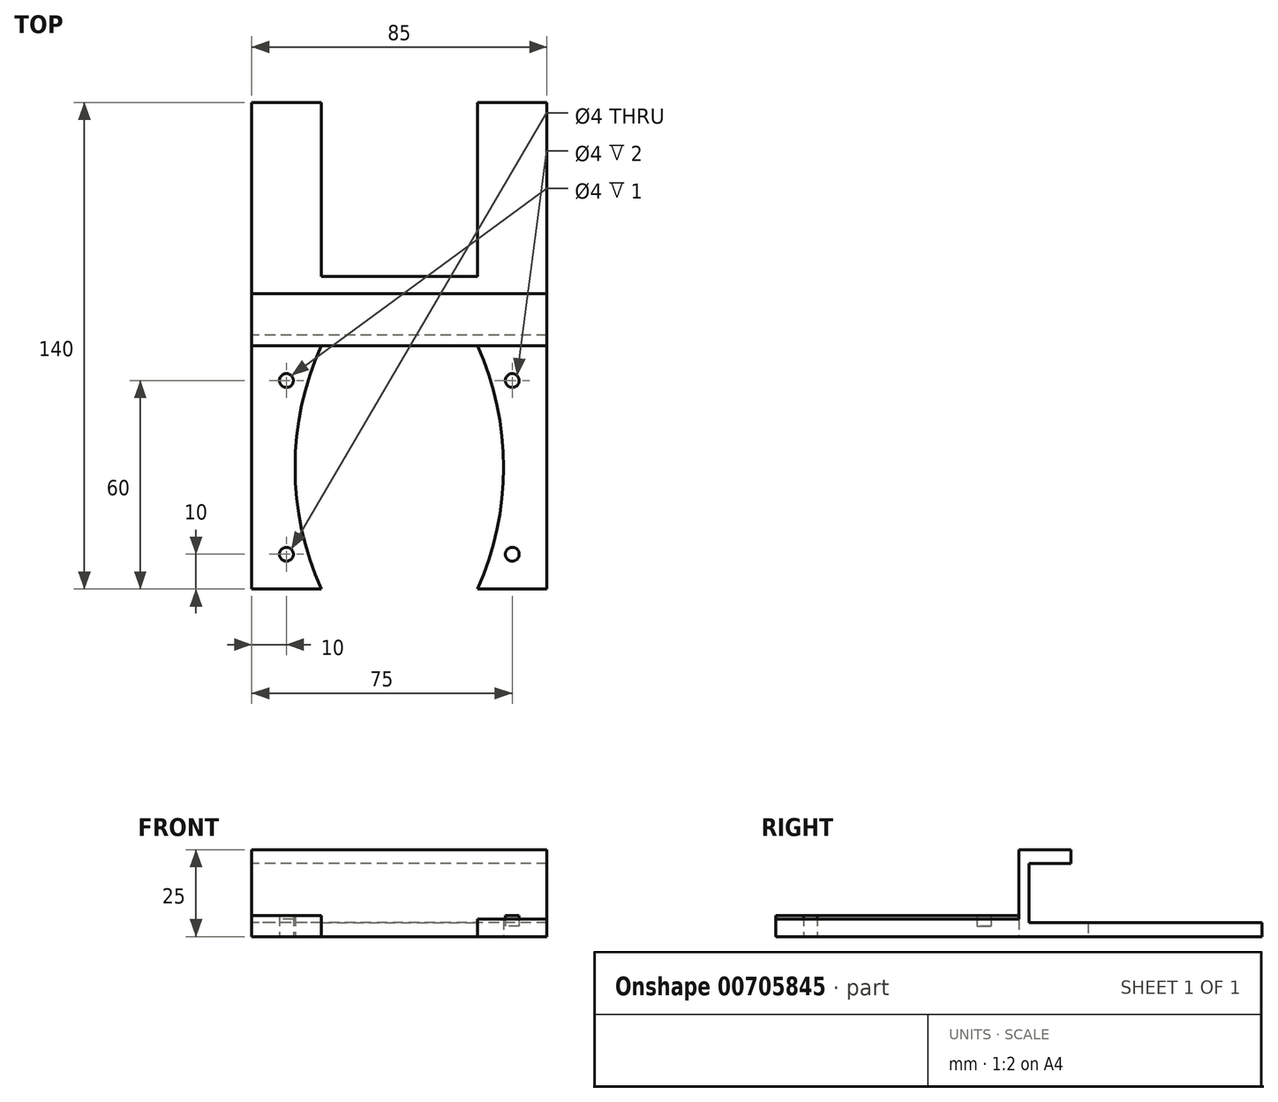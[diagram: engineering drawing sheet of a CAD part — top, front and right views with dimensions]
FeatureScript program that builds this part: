
annotation { "Feature Type Name" : "Feature", "Feature Type Description" : "" }
export const myFeature = defineFeature(function(context is Context, id is Id, definition is map)
    precondition{}
    {
        {
            var Q0;
            Q0=qCreatedBy(makeId("Top.planeOp"),FACE);
            var sketch = newSketch(context, id + "F0", { "sketchPlane" : qUnion([Q0])});
            skLineSegment(sketch, "E0", {"start": v(0, 0) * mm, "end": v(0, 70) * mm, "construction": true});
            skLineSegment(sketch, "E1", {"start": v(0, 0) * mm, "end": v(0, -70) * mm, "construction": true});
            skLineSegment(sketch, "E2", {"start": v(-22.5, 0) * mm, "end": v(22.5, 0) * mm});
            skLineSegment(sketch, "E3", {"start": v(22.5, -70) * mm, "end": v(-22.5, -70) * mm});
            skPoint(sketch, "E4", {"position": v(0, -35) * mm});
            skLineSegment(sketch, "E5", {"start": v(30, -35) * mm, "end": v(-30, -35) * mm, "construction": true});
            skArc(sketch, "E6", {"start": v(-22.5, 0) * mm, "mid": v(-30, -35) * mm, "end": v(-22.5, -70) * mm});
            skLineSegment(sketch, "E7", {"start": v(-22.5, 0) * mm, "end": v(-42.5, 0) * mm});
            skPoint(sketch, "E8", {"position": v(-32.5, 0) * mm});
            skPoint(sketch, "E9", {"position": v(-32.5, -10) * mm});
            skCircle(sketch, "E10", {"center": v(-32.5, -10) * mm, "radius": 2 * mm});
            skCircle(sketch, "E11.MirrorC", {"center": v(-32.5, -60) * mm, "radius": 2 * mm});
            skLineSegment(sketch, "E12.MirrorCS", {"start": v(-22.5, -70) * mm, "end": v(-42.5, -70) * mm});
            skLineSegment(sketch, "E13", {"start": v(-42.5, -70) * mm, "end": v(-42.5, 0) * mm});
            skLineSegment(sketch, "E14.MirrorCS", {"start": v(-42.5, 70) * mm, "end": v(-42.5, 0) * mm});
            skLineSegment(sketch, "E15.MirrorCS", {"start": v(-22.5, 70) * mm, "end": v(-42.5, 70) * mm});
            skLineSegment(sketch, "E16", {"start": v(0, 20) * mm, "end": v(-22.5, 20) * mm});
            skLineSegment(sketch, "E17", {"start": v(-22.5, 20) * mm, "end": v(-22.5, 70) * mm});
            skCircle(sketch, "E18.MirrorC", {"center": v(32.5, -10) * mm, "radius": 2 * mm});
            skLineSegment(sketch, "E19.MirrorCS", {"start": v(22.5, 20) * mm, "end": v(22.5, 70) * mm});
            skPoint(sketch, "E20.MirrorP", {"position": v(32.5, 0) * mm});
            skLineSegment(sketch, "E21.MirrorCS", {"start": v(42.5, 70) * mm, "end": v(42.5, 0) * mm});
            skLineSegment(sketch, "E22.MirrorCS", {"start": v(22.5, 70) * mm, "end": v(42.5, 70) * mm});
            skLineSegment(sketch, "E23.MirrorCS", {"start": v(42.5, -70) * mm, "end": v(42.5, 0) * mm});
            skArc(sketch, "E24.MirrorCS", {"start": v(22.5, 0) * mm, "mid": v(30, -35) * mm, "end": v(22.5, -70) * mm});
            skLineSegment(sketch, "E25.MirrorCS", {"start": v(22.5, -70) * mm, "end": v(42.5, -70) * mm});
            skLineSegment(sketch, "E26.MirrorCS", {"start": v(22.5, 0) * mm, "end": v(42.5, 0) * mm});
            skCircle(sketch, "E27.MirrorC", {"center": v(32.5, -60) * mm, "radius": 2 * mm});
            skLineSegment(sketch, "E28", {"start": v(0, 20) * mm, "end": v(22.5, 20) * mm});
            skSolve(sketch);
        }
        {
            var Q0;
            Q0=makeQuery(id+"F0.imprint","IMPRINT",FACE,{"disambiguationData":[TD([[makeQuery(id+"F0.imprint","IMPRINT",EDGE,{"derivedFrom":sQuery(id+"F0.wireOp",EDGE,"E2")}),1.0]])]});
            extrude(context, id + "F1", {"entities" : qUnion([Q0]), "depth" : 25 * mm, "offsetDistance" : 25 * mm});
        }
        {
            var Q0;
            Q0=makeQuery(id+"F0.imprint","IMPRINT",FACE,{"disambiguationData":[TD([[makeQuery(id+"F0.imprint","IMPRINT",EDGE,{"derivedFrom":sQuery(id+"F0.wireOp",EDGE,"E6")}),-1.0]])]});
            var Q1;
            Q1=makeQuery(id+"F0.imprint","IMPRINT",FACE,{"disambiguationData":[TD([[makeQuery(id+"F0.imprint","IMPRINT",EDGE,{"derivedFrom":sQuery(id+"F0.wireOp",EDGE,"E18.MirrorC")}),1.0]])]});
            extrude(context, id + "F2", {"entities" : qUnion([Q0, Q1]), "operationType" : NewBodyOperationType.ADD, "depth" : 3 * mm, "offsetDistance" : 25 * mm});
        }
        {
            var Q0;
            Q0=makeQuery(id+"F0.imprint","IMPRINT",FACE,{"disambiguationData":[TD([[makeQuery(id+"F0.imprint","IMPRINT",EDGE,{"derivedFrom":sQuery(id+"F0.wireOp",EDGE,"E10")}),1.0]])]});
            var Q1;
            Q1=makeQuery(id+"F0.imprint","IMPRINT",FACE,{"disambiguationData":[TD([[makeQuery(id+"F0.imprint","IMPRINT",EDGE,{"derivedFrom":sQuery(id+"F0.wireOp",EDGE,"E18.MirrorC")}),-1.0]])]});
            extrude(context, id + "F3", {"entities" : qUnion([Q0, Q1]), "operationType" : NewBodyOperationType.ADD, "depth" : 5 * mm, "offsetDistance" : 25 * mm});
        }
        {
            var Q0;
            Q0=makeQuery(id+"F2.boolean.opBoolean","MERGE",FACE,{"derivedFrom":[makeQuery(id+"F1.opExtrude","SWEPT_FACE",FACE,{"disambiguationData":[OSD([sQuery(id+"F0.wireOp",EDGE,"E14.MirrorCS")])]}),makeQuery(id+"F2.opExtrude","SWEPT_FACE",FACE,{"disambiguationData":[OSD([sQuery(id+"F0.wireOp",EDGE,"E13")])]})]});
            var sketch = newSketch(context, id + "F4", { "sketchPlane" : qUnion([Q0])});
            skLineSegment(sketch, "E29.0", {"start": v(-70, 25) * mm, "end": v(-70, 0) * mm});
            skLineSegment(sketch, "E29.1", {"start": v(-70, 25) * mm, "end": v(0, 25) * mm});
            skLineSegment(sketch, "E29.2", {"start": v(0, 25) * mm, "end": v(0, 0) * mm});
            skLineSegment(sketch, "E29.3", {"start": v(-70, 0) * mm, "end": v(70, 0) * mm});
            skPoint(sketch, "E30.orphan", {"position": v(0, 3) * mm});
            skLineSegment(sketch, "E31", {"start": v(-70, 21) * mm, "end": v(-3, 21) * mm});
            skLineSegment(sketch, "E32", {"start": v(-3, 21) * mm, "end": v(-3, 4) * mm});
            skLineSegment(sketch, "E33", {"start": v(-3, 4) * mm, "end": v(-70, 4) * mm});
            skPoint(sketch, "E34", {"position": v(-3, 12.5) * mm});
            skLineSegment(sketch, "E35", {"start": v(-3, 12.5) * mm, "end": v(-7.34, 12.5) * mm, "construction": true});
            skLineSegment(sketch, "E36", {"start": v(-15, 21) * mm, "end": v(-15, 25) * mm});
            skSolve(sketch);
        }
        {
            var Q0;
            {var subQ0=sQuery(id+"F4.wireOp",EDGE,"E31");Q0=makeQuery(id+"F4.imprint","IMPRINT",FACE,{"disambiguationData":[TD([[makeQuery(id+"F4.imprint","IMPRINT",EDGE,{"derivedFrom":subQ0}),-1.0]])]});}
            var Q1;
            {var subQ5=sQuery(id+"F4.wireOp",EDGE,"E36");Q1=makeQuery(id+"F4.imprint","IMPRINT",FACE,{"disambiguationData":[TD([[makeQuery(id+"F4.imprint","IMPRINT",EDGE,{"derivedFrom":subQ5}),1.0]])]});}
            extrude(context, id + "F5", {"entities" : qUnion([Q0, Q1]), "operationType" : NewBodyOperationType.REMOVE, "endBound" : BoundingType.THROUGH_ALL, "oppositeDirection" : true, "depth" : 25 * mm, "offsetDistance" : 25 * mm});
        }
        {
            var Q0;
            Q0=makeQuery(id+"F0.imprint","IMPRINT",FACE,{"disambiguationData":[TD([[makeQuery(id+"F0.imprint","IMPRINT",EDGE,{"derivedFrom":sQuery(id+"F0.wireOp",EDGE,"E11.MirrorC")}),-1.0]])]});
            var Q1;
            Q1=makeQuery(id+"F0.imprint","IMPRINT",FACE,{"disambiguationData":[TD([[makeQuery(id+"F0.imprint","IMPRINT",EDGE,{"derivedFrom":sQuery(id+"F0.wireOp",EDGE,"E27.MirrorC")}),1.0]])]});
            extrude(context, id + "F6", {"entities" : qUnion([Q0, Q1]), "operationType" : NewBodyOperationType.ADD, "depth" : 6 * mm, "offsetDistance" : 25 * mm});
        }
    });
